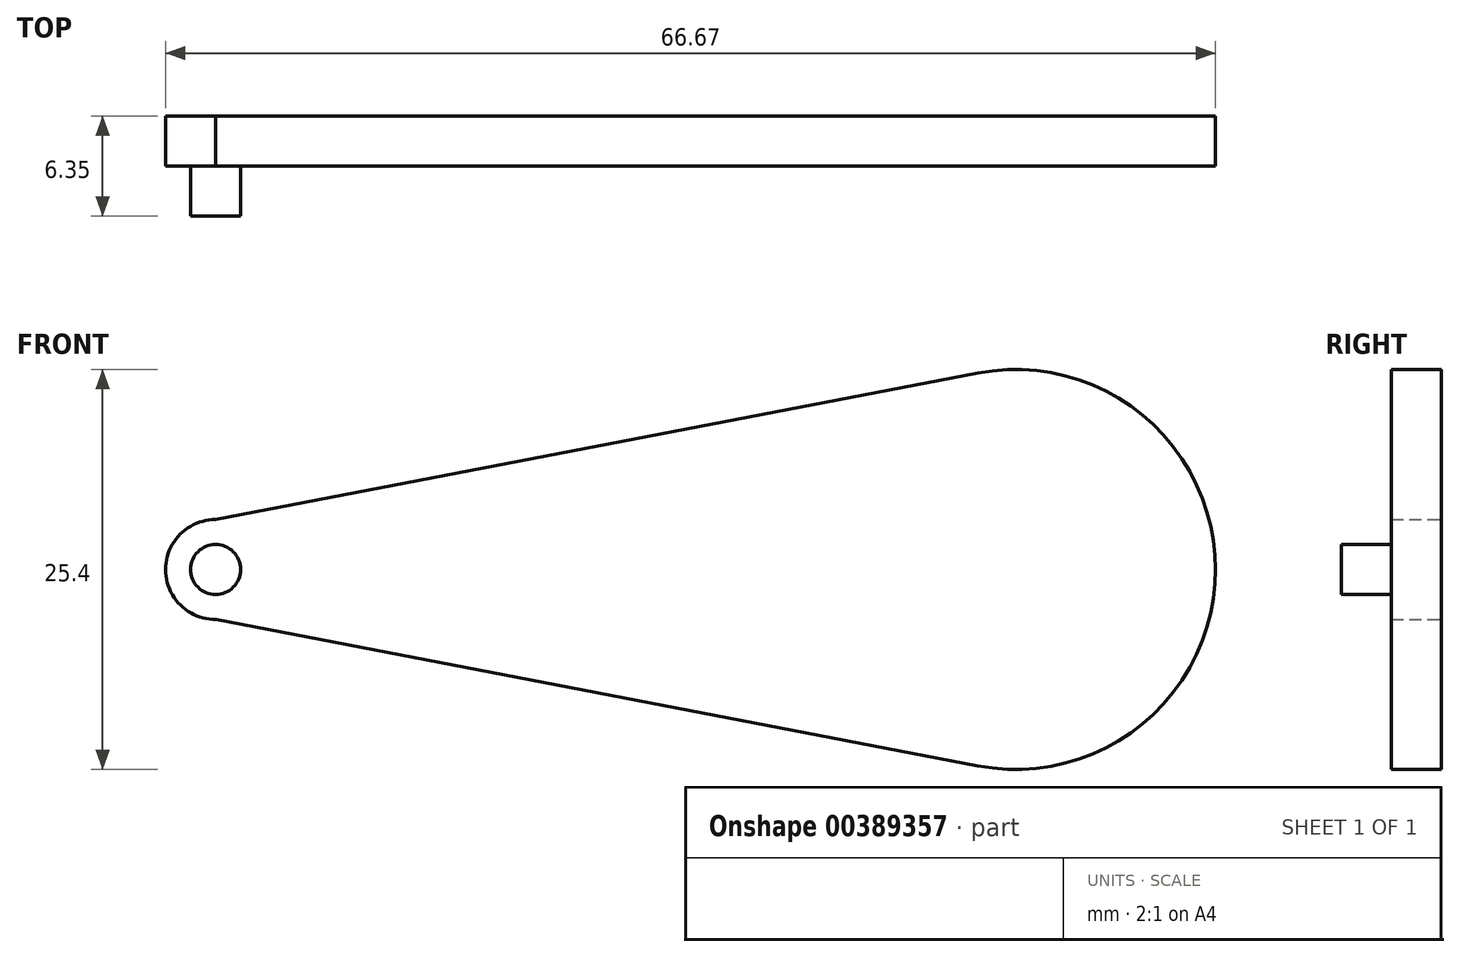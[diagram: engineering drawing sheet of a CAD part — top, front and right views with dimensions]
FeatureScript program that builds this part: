
annotation { "Feature Type Name" : "Feature", "Feature Type Description" : "" }
export const myFeature = defineFeature(function(context is Context, id is Id, definition is map)
    precondition{}
    {
        {
            var Q0;
            Q0=qCreatedBy(makeId("Front.planeOp"),FACE);
            var sketch = newSketch(context, id + "F0", { "sketchPlane" : qUnion([Q0])});
            skCircle(sketch, "E0", {"center": v(0, 0) * mm, "radius": 12.7 * mm});
            skCircle(sketch, "E1", {"center": v(-50.8, 0) * mm, "radius": 3.18 * mm});
            skLineSegment(sketch, "E2", {"start": v(-50.8, 3.18) * mm, "end": v(0, 12.93) * mm});
            skLineSegment(sketch, "E3", {"start": v(-50.78, -3.17) * mm, "end": v(0, -12.93) * mm});
            skSolve(sketch);
        }
        {
            var Q0;
            Q0 = qSketchRegion(id + "F0", true);
            extrude(context, id + "F1", {"entities" : qUnion([Q0]), "depth" : 3.17 * mm});
        }
        {
            var Q0;
            Q0=makeQuery(id+"F1.opExtrude","CAP_FACE",FACE,{"disambiguationData":[OSD([sQuery(id+"F0.wireOp",EDGE,"E0"),sQuery(id+"F0.wireOp",EDGE,"E1"),sQuery(id+"F0.wireOp",EDGE,"E2"),sQuery(id+"F0.wireOp",EDGE,"E3")])],"isStart":false});
            var sketch = newSketch(context, id + "F2", { "sketchPlane" : qUnion([Q0])});
            skCircle(sketch, "E4", {"center": v(-50.8, 0) * mm, "radius": 1.59 * mm});
            skSolve(sketch);
        }
        {
            var Q0;
            Q0=makeQuery(id+"F2.imprint","IMPRINT",FACE,{"disambiguationData":[TD([[makeQuery(id+"F2.imprint","IMPRINT",EDGE,{"derivedFrom":sQuery(id+"F2.wireOp",EDGE,"E4")}),1.0]])]});
            extrude(context, id + "F3", {"entities" : qUnion([Q0]), "operationType" : NewBodyOperationType.ADD, "depth" : 3.17 * mm});
        }
    });
